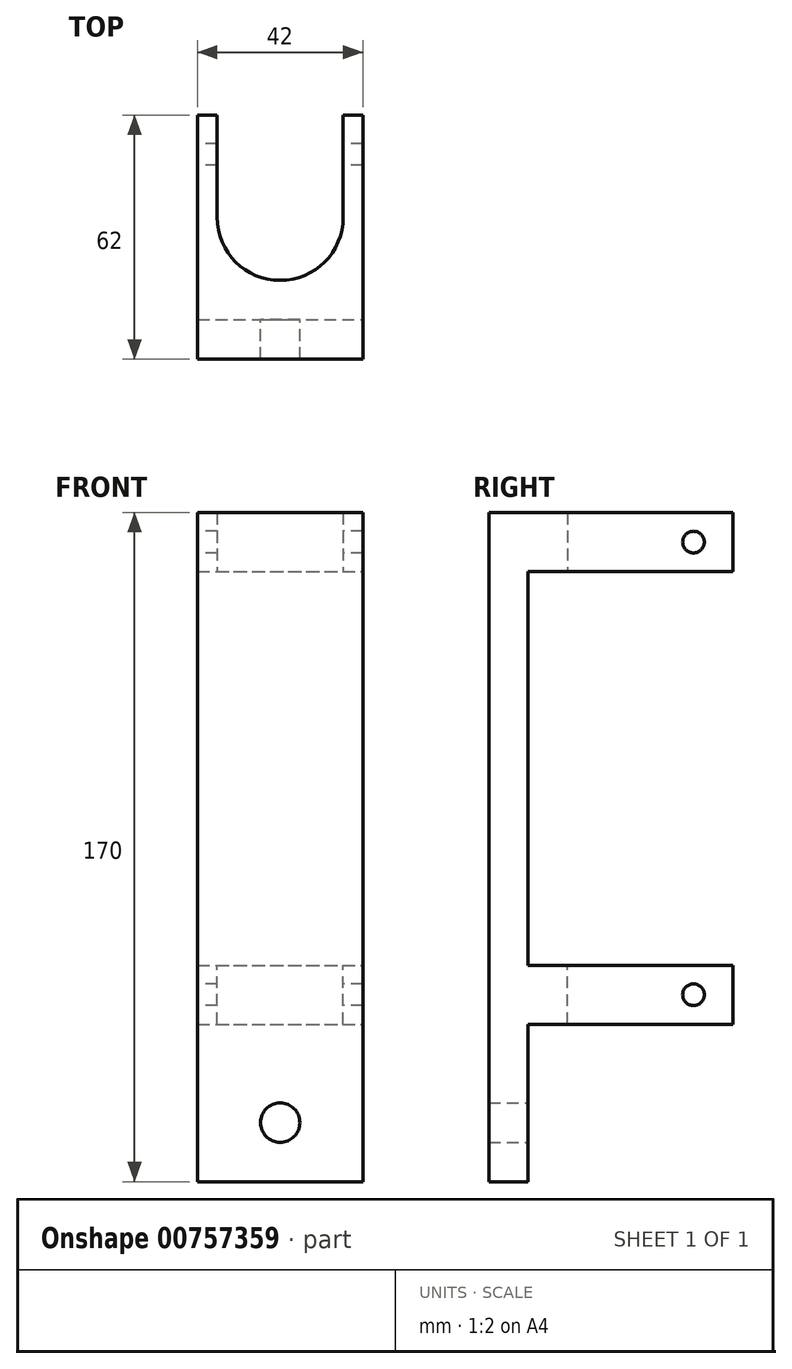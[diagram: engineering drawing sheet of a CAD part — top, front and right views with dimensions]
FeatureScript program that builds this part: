
annotation { "Feature Type Name" : "Feature", "Feature Type Description" : "" }
export const myFeature = defineFeature(function(context is Context, id is Id, definition is map)
    precondition{}
    {
        {
            var Q0;
            Q0=qCreatedBy(makeId("Top.planeOp"),FACE);
            var sketch = newSketch(context, id + "F0", { "sketchPlane" : qUnion([Q0])});
            skLineSegment(sketch, "E0.bottom", {"start": v(-21, 26) * mm, "end": v(21, 26) * mm});
            skLineSegment(sketch, "E0.top", {"start": v(-21, -26) * mm, "end": v(21, -26) * mm});
            skLineSegment(sketch, "E0.left", {"start": v(-21, 26) * mm, "end": v(-21, -26) * mm});
            skLineSegment(sketch, "E0.right", {"start": v(21, 26) * mm, "end": v(21, -26) * mm});
            skSolve(sketch);
        }
        {
            var Q0;
            Q0 = qSketchRegion(id + "F0", true);
            extrude(context, id + "F1", {"entities" : qUnion([Q0]), "depth" : 15 * mm, "offsetDistance" : 25 * mm});
        }
        {
            var Q0;
            Q0=makeQuery(id+"F1.opExtrude","CAP_FACE",FACE,{"disambiguationData":[OSD([sQuery(id+"F0.wireOp",EDGE,"E0.bottom"),sQuery(id+"F0.wireOp",EDGE,"E0.top"),sQuery(id+"F0.wireOp",EDGE,"E0.left"),sQuery(id+"F0.wireOp",EDGE,"E0.right")])],"isStart":false});
            var sketch = newSketch(context, id + "F2", { "sketchPlane" : qUnion([Q0])});
            skArc(sketch, "E1", {"start": v(-16, 0) * mm, "mid": v(0, -16) * mm, "end": v(16, 0) * mm});
            skLineSegment(sketch, "E2", {"start": v(-16, 0) * mm, "end": v(-16, 26) * mm});
            skLineSegment(sketch, "E3", {"start": v(16, 0) * mm, "end": v(16, 26) * mm});
            skLineSegment(sketch, "E4", {"start": v(16, 26) * mm, "end": v(-16, 26) * mm});
            skSolve(sketch);
        }
        {
            var Q0;
            Q0 = qSketchRegion(id + "F2", true);
            extrude(context, id + "F3", {"entities" : qUnion([Q0]), "operationType" : NewBodyOperationType.REMOVE, "oppositeDirection" : true, "depth" : 50 * mm, "offsetDistance" : 25 * mm});
        }
        {
            var Q0;
            Q0=makeQuery(id+"F1.opExtrude","CAP_FACE",FACE,{"disambiguationData":[OSD([sQuery(id+"F0.wireOp",EDGE,"E0.bottom"),sQuery(id+"F0.wireOp",EDGE,"E0.top"),sQuery(id+"F0.wireOp",EDGE,"E0.left"),sQuery(id+"F0.wireOp",EDGE,"E0.right")])],"isStart":false});
            var sketch = newSketch(context, id + "F4", { "sketchPlane" : qUnion([Q0])});
            skLineSegment(sketch, "E5.bottom", {"start": v(-21, -26) * mm, "end": v(21, -26) * mm});
            skLineSegment(sketch, "E5.top", {"start": v(-21, -16) * mm, "end": v(21, -16) * mm});
            skLineSegment(sketch, "E5.left", {"start": v(-21, -26) * mm, "end": v(-21, -16) * mm});
            skLineSegment(sketch, "E5.right", {"start": v(21, -26) * mm, "end": v(21, -16) * mm});
            skSolve(sketch);
        }
        {
            var Q0;
            Q0 = qSketchRegion(id + "F4", true);
            extrude(context, id + "F5", {"entities" : qUnion([Q0]), "operationType" : NewBodyOperationType.ADD, "depth" : 100 * mm, "offsetDistance" : 25 * mm});
        }
        {
            var Q0;
            Q0=makeQuery(id+"F5.opExtrude","CAP_FACE",FACE,{"disambiguationData":[OSD([sQuery(id+"F4.wireOp",EDGE,"E5.bottom"),sQuery(id+"F4.wireOp",EDGE,"E5.top"),sQuery(id+"F4.wireOp",EDGE,"E5.left"),sQuery(id+"F4.wireOp",EDGE,"E5.right")])],"isStart":false});
            var sketch = newSketch(context, id + "F6", { "sketchPlane" : qUnion([Q0])});
            skLineSegment(sketch, "E6.bottom", {"start": v(-21, 26) * mm, "end": v(21, 26) * mm});
            skLineSegment(sketch, "E6.top", {"start": v(-21, -26) * mm, "end": v(21, -26) * mm});
            skLineSegment(sketch, "E6.left", {"start": v(-21, 26) * mm, "end": v(-21, -26) * mm});
            skLineSegment(sketch, "E6.right", {"start": v(21, 26) * mm, "end": v(21, -26) * mm});
            skSolve(sketch);
        }
        {
            var Q0;
            Q0 = qSketchRegion(id + "F6", true);
            extrude(context, id + "F7", {"entities" : qUnion([Q0]), "operationType" : NewBodyOperationType.ADD, "depth" : 15 * mm, "offsetDistance" : 25 * mm});
        }
        {
            var Q0;
            Q0 = qSketchRegion(id + "F2", true);
            extrude(context, id + "F8", {"entities" : qUnion([Q0]), "operationType" : NewBodyOperationType.REMOVE, "depth" : 200 * mm, "offsetDistance" : 25 * mm});
        }
        {
            var Q0;
            Q0=makeQuery(id+"F7.opExtrude","CAP_FACE",FACE,{"disambiguationData":[OSD([sQuery(id+"F6.wireOp",EDGE,"E6.bottom"),sQuery(id+"F6.wireOp",EDGE,"E6.top"),sQuery(id+"F6.wireOp",EDGE,"E6.left"),sQuery(id+"F6.wireOp",EDGE,"E6.right")])],"isStart":false});
            var sketch = newSketch(context, id + "F9", { "sketchPlane" : qUnion([Q0])});
            skLineSegment(sketch, "E7.bottom", {"start": v(-21, -26) * mm, "end": v(21, -26) * mm});
            skLineSegment(sketch, "E7.top", {"start": v(-21, -36) * mm, "end": v(21, -36) * mm});
            skLineSegment(sketch, "E7.left", {"start": v(-21, -26) * mm, "end": v(-21, -36) * mm});
            skLineSegment(sketch, "E7.right", {"start": v(21, -26) * mm, "end": v(21, -36) * mm});
            skSolve(sketch);
        }
        {
            var Q0;
            Q0 = qSketchRegion(id + "F9", true);
            extrude(context, id + "F10", {"entities" : qUnion([Q0]), "operationType" : NewBodyOperationType.ADD, "oppositeDirection" : true, "depth" : 170 * mm, "offsetDistance" : 25 * mm});
        }
        {
            var Q0;
            Q0=makeQuery(id+"F10.opExtrude","SWEPT_FACE",FACE,{"disambiguationData":[OSD([sQuery(id+"F9.wireOp",EDGE,"E7.bottom")])]});
            var sketch = newSketch(context, id + "F11", { "sketchPlane" : qUnion([Q0])});
            skCircle(sketch, "E8", {"center": v(0, -25) * mm, "radius": 5 * mm});
            skSolve(sketch);
        }
        {
            var Q0;
            Q0 = qSketchRegion(id + "F11", true);
            extrude(context, id + "F12", {"entities" : qUnion([Q0]), "operationType" : NewBodyOperationType.REMOVE, "oppositeDirection" : true, "depth" : 25 * mm, "offsetDistance" : 25 * mm});
        }
        {
            var Q0;
            Q0=makeQuery(id+"F10.opExtrude","SWEPT_FACE",FACE,{"disambiguationData":[OSD([sQuery(id+"F9.wireOp",EDGE,"E7.left")])]});
            var sketch = newSketch(context, id + "F13", { "sketchPlane" : qUnion([Q0])});
            skCircle(sketch, "E9", {"center": v(-16, 122.5) * mm, "radius": 2.75 * mm});
            skCircle(sketch, "E10", {"center": v(-16, 7.5) * mm, "radius": 2.75 * mm});
            skSolve(sketch);
        }
        {
            var Q0;
            Q0 = qSketchRegion(id + "F13", true);
            extrude(context, id + "F14", {"entities" : qUnion([Q0]), "operationType" : NewBodyOperationType.REMOVE, "endBound" : BoundingType.SYMMETRIC, "oppositeDirection" : true, "depth" : 200 * mm, "offsetDistance" : 25 * mm});
        }
        {
            var Q0;
            Q0=makeQuery(id+"F10.boolean.opBoolean","MERGE",FACE,{"derivedFrom":[makeQuery(id+"F7.boolean.opBoolean","MERGE",FACE,{"derivedFrom":[makeQuery(id+"F5.boolean.opBoolean","MERGE",FACE,{"derivedFrom":[makeQuery(id+"F1.opExtrude","SWEPT_FACE",FACE,{"disambiguationData":[OSD([sQuery(id+"F0.wireOp",EDGE,"E0.right")])]}),makeQuery(id+"F5.opExtrude","SWEPT_FACE",FACE,{"disambiguationData":[OSD([sQuery(id+"F4.wireOp",EDGE,"E5.right")])]})]}),makeQuery(id+"F7.opExtrude","SWEPT_FACE",FACE,{"disambiguationData":[OSD([sQuery(id+"F6.wireOp",EDGE,"E6.right")])]})]}),makeQuery(id+"F10.opExtrude","SWEPT_FACE",FACE,{"disambiguationData":[OSD([sQuery(id+"F9.wireOp",EDGE,"E7.right")])]})]});
            var sketch = newSketch(context, id + "F15", { "sketchPlane" : qUnion([Q0])});
            skLineSegment(sketch, "E11.bottom", {"start": v(-16, 115) * mm, "end": v(-26, 115) * mm});
            skLineSegment(sketch, "E11.top", {"start": v(-16, 15) * mm, "end": v(-26, 15) * mm});
            skLineSegment(sketch, "E11.left", {"start": v(-16, 115) * mm, "end": v(-16, 15) * mm});
            skLineSegment(sketch, "E11.right", {"start": v(-26, 115) * mm, "end": v(-26, 15) * mm});
            skSolve(sketch);
        }
        {
            var Q0;
            Q0 = qSketchRegion(id + "F15", true);
            extrude(context, id + "F16", {"entities" : qUnion([Q0]), "operationType" : NewBodyOperationType.REMOVE, "oppositeDirection" : true, "depth" : 60 * mm, "offsetDistance" : 25 * mm});
        }
    });
